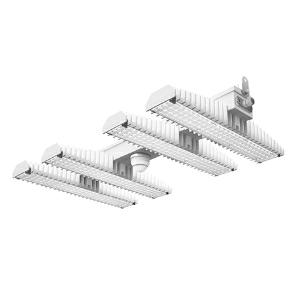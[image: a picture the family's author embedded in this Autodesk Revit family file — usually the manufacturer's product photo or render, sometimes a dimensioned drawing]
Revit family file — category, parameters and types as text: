
# Revit family: 3f_filippi_-_3f_lem_sensor_ampio_3f_filippi_-_59255_a0811_-_3f_lem_4_led_200_dali_sensor_cr_ampio___vt_00b7
name_source: partatom
category: Lighting Fixtures
units: mm (PartAtom-declared; Revit-internal decimal feet)

## family parameters
Cut with Voids When Loaded = No
Host = Face
Light Source = No
Part Type = Normal
Room Calculation Point = No
Round Connector Dimension = Use Diameter
Shared = No

## types (1)
- 3F Filippi - 3F LEM Sensor Ampio (1 x LED, 31641 lm, 219 W, 4000 K)
    Apparent Load = 219 VA
    Approval mark = ENEC
    CIE Flux Codes = 60 92 99 100 100
    Color Rendering = 80
    Color Temperature = 4000 K
    Control Gear = Electronic transformer
    Default Elevation = 1800 mm
    Description = Industrial luminaire with high light output and high luminous efficiency designed with the most innovative technologies for environments with temperature up to 50°C.

ILLUMINOTECHNICAL
Luminous efficiency 100% (DLOR 99%, ULOR 1%).
Initial luminous flux of the luminaire 31641 lm.
Direct symmetric wide distribution: the illuminated area has a rectangular shape.
Installation Interdistance Transv.D = 1.58 x hu - Long.D = 1.45 x hu.
Tabular UGR (CIE 117 - 4H-8H; S=0.25H; 70/50/20): RUG 22.9 - 23.9.
Beam angle: 93° - 99°.
Luminous efficacy 144 lm/W.
Lifetime (L93/B10): 30000 h. (tq+25°C)
Lifetime (L90/B10): 50000 h. (tq+25°C)
Lifetime (L85/B10): 80000 h. (tq+25°C)
Lifetime (L80/B10): 100000 h. (tq+25°C)
Lifetime (L85/B10): 50000 h. (tq+50°C)
Sudden decreased luminous flux after 50000 hours: 0% (C0).
Photobiological safety in compliance with IEC/TR 62778: RG0 risk exempt, (IEC 62471).
In compliance with IEC/EN 62722-2-1 - IEC/EN 62717 standards.

SOURCE
4 Mid-Power linear LED modules 50W/840.
Energy efficiency class (UE 2019/2020 - UE 2019/2015): C.
CIE 13.3 Colour rendering index: CRI >80 (R9 <50%).
IES TM-30 Fidelity Index: Rf = 84 Rg = 95.
CCT nominal colour temperature 4000 K.
Colour initial tolerance (MacAdam): SDCM 3.

MECHANICAL
Passive modular heatsinks in die-casted aluminium, painted in white colour.
To optimize the thermal management of the LED module, the heatsinks are oversized and provided with self-cleaning of cooling fins.
Wiring body in aluminium and galvanised steel anchored solidly to the sinks and thermally separated.
3F Lens lenses with high luminous efficiency, transparent methacrylate (PMMA), fixed to the LED modules.
Fixing brackets in stainless steel.
Luminaire with limited surface temperature. - D - (EN 60598-2-24)
Dimensions: 952x542 mm, height 133 mm. Weight 19.988 kg.
IP54 protection degree.
Mechanical strength to impacts IK04 (0.5 joule).
Glow-wire test resistance 650°C.

ELECTRICAL
Halogen Free DALI electronic wiring 230V-50/60Hz, power factor 0.90 at full load, THD <25%, constant output current, class I, 2 driver, 2 DALI addresses.
DALI light and presence sensor integrated in the luminarie.
Power of the luminaire 219 W.
CE - IEC 60598-1 - EN 60598-1.
Flicker: <4%.
Ambient temperature from -25°C to +50°C.
Temperature class T6 max 85°C.
Quick connection via M25 5P connector with 9-13 mm tightening range.
Power unit positioned on a separate compartment by the LED module to ensure optimum temperatures of cabling components, to be inspectable and maintainable.
Relative humidity UR: <85%.

INSTALLATION
Ceiling / Suspended / Wall.
All accessories dedicated to this product are available on the Catalog and on our website www.3F-Filippi.com.

ACCESSORIES
A0811 - VT transparent glass, tempered, not flammable, with sealing gasket.
One required for each light module. The pack contains 10 pieces.

APPLICATIONS
In commercial environments, exhibition and industrial areas, stores, open areas.
Applications with high ambient temperature up to 50°C.
Environments in which it is necessary a total protection against falling fragments (eg environments with foodstuffs or machines with moving parts or with extreme temperature changes), use luminaires with polycarbonate lenses.

LIGHT MANAGEMENT
The DALI presence and brightness sensor, integrated in the luminaire, allows you to keep the level of illumination constant as a function of natural light (in addition to switching on/off as a result of presence detection and set twilight threshold).
Recommended installation height up to 10 m.
Commissioning of the control system via free APP; the intervention of a specialist technician can be quoted on request.

WARNING
The luminaire cannot be controlled manually with PUSH-DIM technology.
Fixture not suitable for cold stores with an ambient temperature <0°C and/or relative humidity >85%.
Luminaire designed for disposal/recycling at end-of-life.
Replaceable (LED only) light source by a professional. Replaceable control gear by a professional.
    Height = 133 mm  [stored 0.436352 ft]
    Lamp = 1 x LED
    Lamp Light Flux = 31641 lm
    Lamp Power = 219 W
    Lamp count = 1
    Length = 952 mm
    Lifetime = 50000 h
    Luminous efficacy = 144 lm/W
    Manufacturer = 3F Filippi
    ModVariant = No
    Model = 3F Filippi - 59255+A0811 - 3F LEM 4 LED 200 DALI Sensor CR AMPIO + VT
    Mounting Place = Ceiling
    Mounting Type = Pendant
    Number of Poles = 1
    OnlyDefault = Yes
    Power Factor = 1
    Product Name = 3F Filippi - 3F LEM Sensor Ampio
    Product group = pendant luminaire
    ProductGroupID = 9
    Protection Class = Protection class I
    Protection Degree = IP 54
    RLX_Detail_Level = 1
    RLX_Emergency_Light_Flux = 0 lm
    RLX_Emergency_Type = 0
    RLX_Emergency_Type_DB = No
    RlxData = <blob elided: 123733 chars, md5=ddd9136d>
    Socket = socket
    Standby Power = 0 W
    System Light Flux = 31641 lm
    System Power = 219 W
    Type Comments = Product without accessories
    Type Image = 3f_filippi_-_lem_4_sensor__a0811.jpg
    URL = http://relux.com
    VarID = ---
    Voltage = 0 V
    Weight = 0.00 kg
    Width = 542 mm

note: [stored X ft] marks values corroborated as IEEE doubles in the binary element streams (Revit-internal decimal feet)

## geometry (parser evidence)
native form markers: Blend x4, Sweep x9
no freeform markers — native parametric forms only
